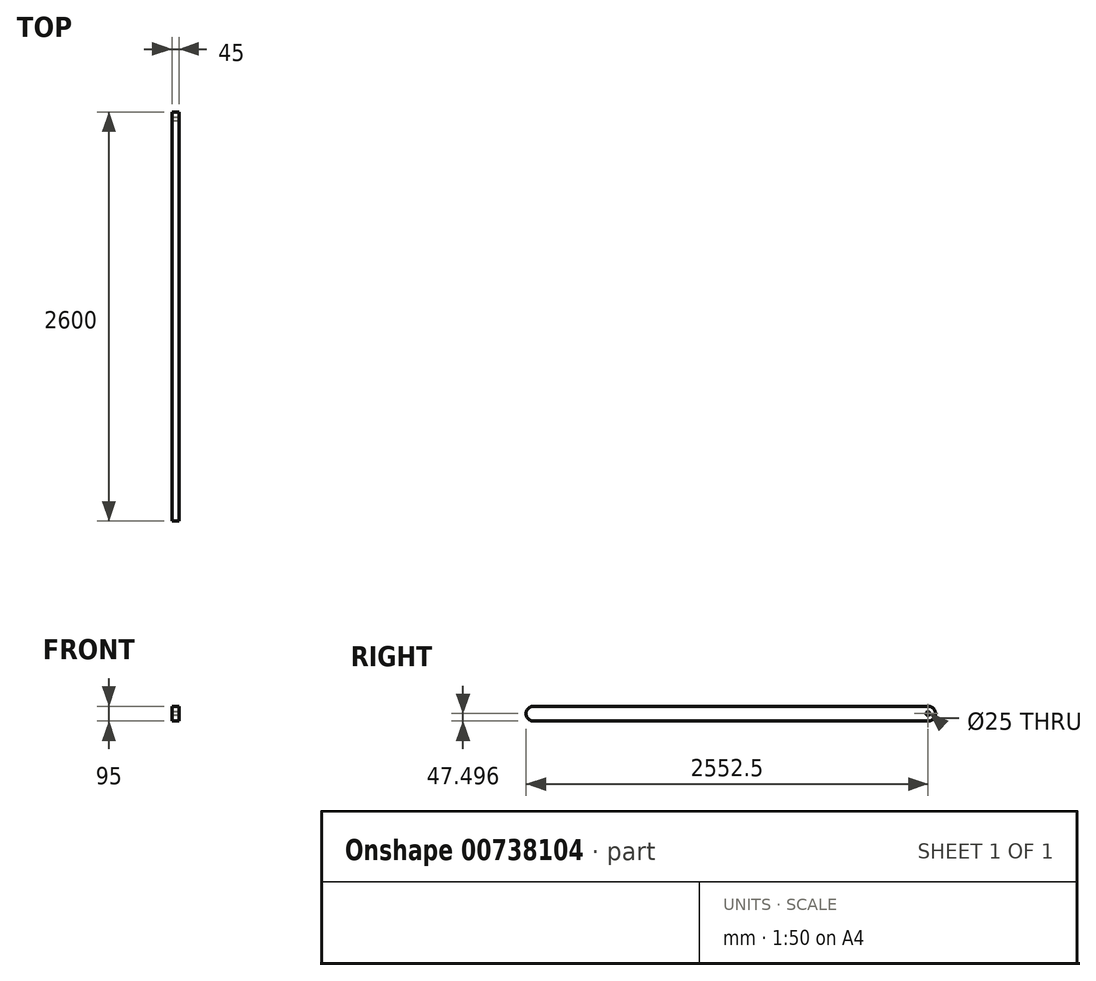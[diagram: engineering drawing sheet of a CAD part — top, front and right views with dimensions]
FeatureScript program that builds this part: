
annotation { "Feature Type Name" : "Feature", "Feature Type Description" : "" }
export const myFeature = defineFeature(function(context is Context, id is Id, definition is map)
    precondition{}
    {
        {
            var Q0;
            Q0=qCreatedBy(makeId("Right.planeOp"),FACE);
            var sketch = newSketch(context, id + "F0", { "sketchPlane" : qUnion([Q0])});
            skLineSegment(sketch, "E0.bottom", {"start": v(-69.6, 49.04) * mm, "end": v(2530.4, 49.04) * mm});
            skLineSegment(sketch, "E0.top", {"start": v(-69.6, -45.96) * mm, "end": v(2530.4, -45.96) * mm});
            skPoint(sketch, "E1", {"position": v(2435.4, 49.04) * mm});
            skCircle(sketch, "E2", {"center": v(2482.9, 1.54) * mm, "radius": 12.5 * mm});
            skPoint(sketch, "E3", {"position": v(2482.9, 49.04) * mm});
            skArc(sketch, "E4", {"start": v(2482.9, -45.96) * mm, "mid": v(2530.4, 1.54) * mm, "end": v(2482.9, 49.04) * mm});
            skPoint(sketch, "E5", {"position": v(-22.1, 49.04) * mm});
            skArc(sketch, "E6", {"start": v(-22.1, 49.04) * mm, "mid": v(-69.6, 1.54) * mm, "end": v(-22.1, -45.96) * mm});
            skSolve(sketch);
        }
        {
            var Q0;
            Q0=makeQuery(id+"F0.imprint","IMPRINT",FACE,{"disambiguationData":[TD([[makeQuery(id+"F0.imprint","IMPRINT",EDGE,{"derivedFrom":sQuery(id+"F0.wireOp",EDGE,"E2")}),-1.0]])]});
            extrude(context, id + "F1", {"entities" : qUnion([Q0]), "depth" : 45 * mm, "offsetDistance" : 25 * mm});
        }
    });
